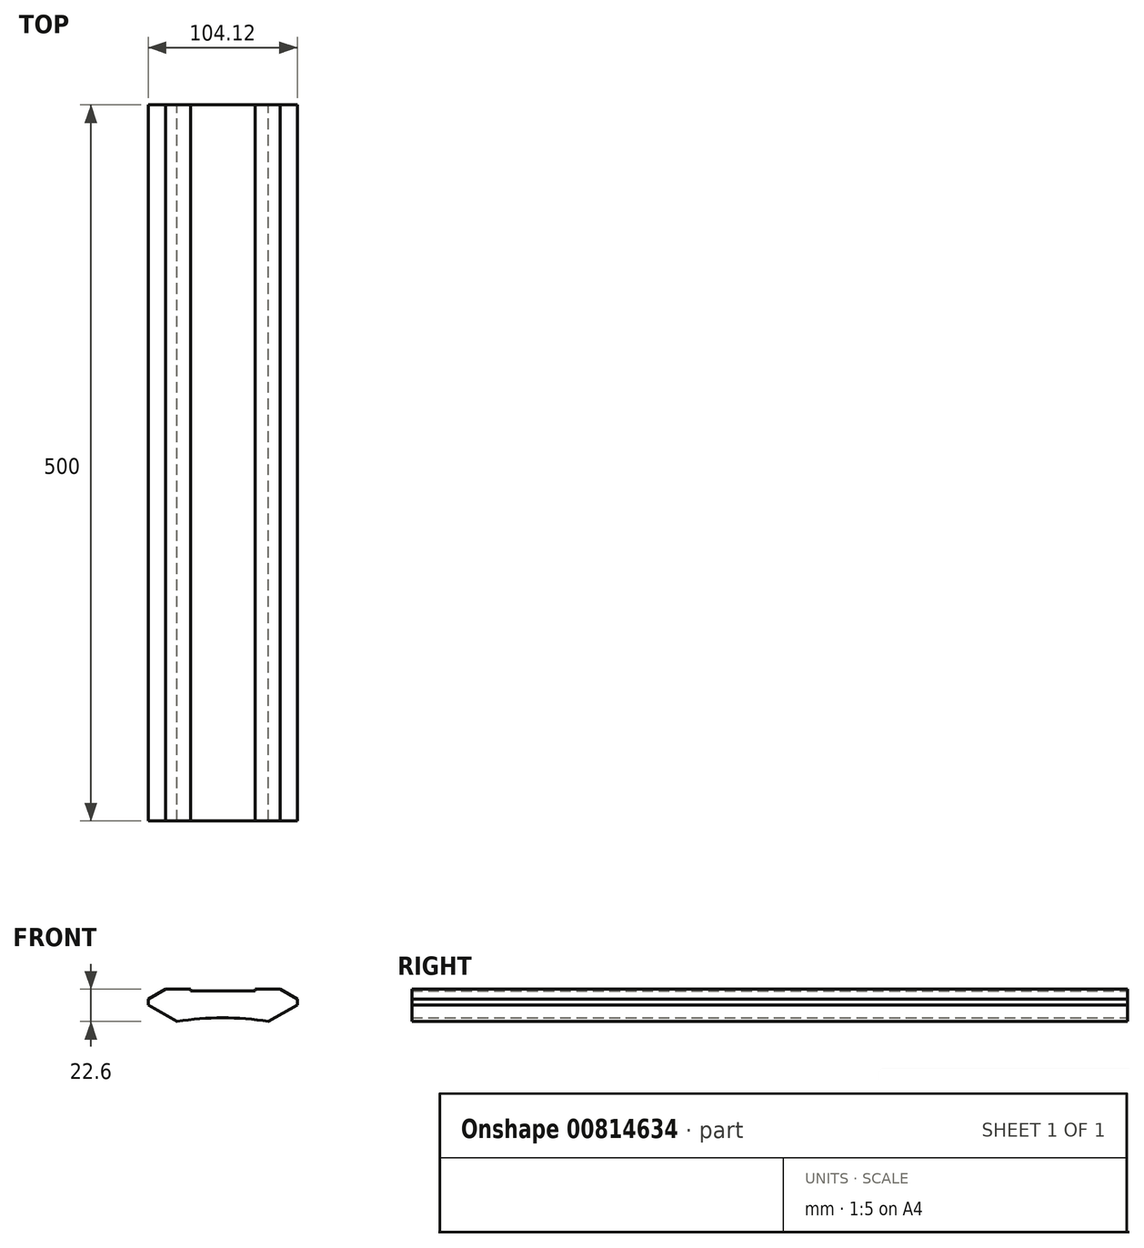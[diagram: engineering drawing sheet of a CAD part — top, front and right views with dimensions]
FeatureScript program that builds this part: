
annotation { "Feature Type Name" : "Feature", "Feature Type Description" : "" }
export const myFeature = defineFeature(function(context is Context, id is Id, definition is map)
    precondition{}
    {
        {
            var Q0;
            Q0=qCreatedBy(makeId("Front.planeOp"),FACE);
            var sketch = newSketch(context, id + "F0", { "sketchPlane" : qUnion([Q0])});
            skLineSegment(sketch, "E0", {"start": v(0, 33.16) * mm, "end": v(0, -46.31) * mm, "construction": true});
            skLineSegment(sketch, "E1", {"start": v(0, 9.67) * mm, "end": v(22.5, 9.67) * mm});
            skLineSegment(sketch, "E2", {"start": v(22.5, 9.67) * mm, "end": v(22.5, 10.97) * mm});
            skLineSegment(sketch, "E3", {"start": v(22.5, 10.97) * mm, "end": v(39.98, 10.97) * mm});
            skLineSegment(sketch, "E4", {"start": v(39.98, 10.97) * mm, "end": v(52.06, 4) * mm});
            skLineSegment(sketch, "E5", {"start": v(52.06, 4) * mm, "end": v(52.06, 0) * mm});
            skLineSegment(sketch, "E6", {"start": v(52.06, 0) * mm, "end": v(31.9, -11.63) * mm});
            skLineSegment(sketch, "E7.MirrorCS", {"start": v(0, 9.67) * mm, "end": v(-22.5, 9.67) * mm});
            skLineSegment(sketch, "E8.MirrorCS", {"start": v(-22.5, 9.67) * mm, "end": v(-22.5, 10.97) * mm});
            skLineSegment(sketch, "E9.MirrorCS", {"start": v(-22.5, 10.97) * mm, "end": v(-39.98, 10.97) * mm});
            skLineSegment(sketch, "E10.MirrorCS", {"start": v(-39.98, 10.97) * mm, "end": v(-52.06, 4) * mm});
            skLineSegment(sketch, "E11.MirrorCS", {"start": v(-52.06, 4) * mm, "end": v(-52.06, 0) * mm});
            skLineSegment(sketch, "E12.MirrorCS", {"start": v(-52.06, 0) * mm, "end": v(-31.9, -11.63) * mm});
            skArc(sketch, "E13", {"start": v(31.9, -11.63) * mm, "mid": v(0, -9.07) * mm, "end": v(-31.9, -11.63) * mm});
            skSolve(sketch);
        }
        {
            var Q0;
            Q0=makeQuery(id+"F0.imprint","IMPRINT",FACE,{"disambiguationData":[TD([[makeQuery(id+"F0.imprint","IMPRINT",EDGE,{"derivedFrom":sQuery(id+"F0.wireOp",EDGE,"E1")}),-1.0]])]});
            extrude(context, id + "F1", {"entities" : qUnion([Q0]), "endBound" : BoundingType.SYMMETRIC, "depth" : 500 * mm, "offsetDistance" : 25 * mm});
        }
    });
